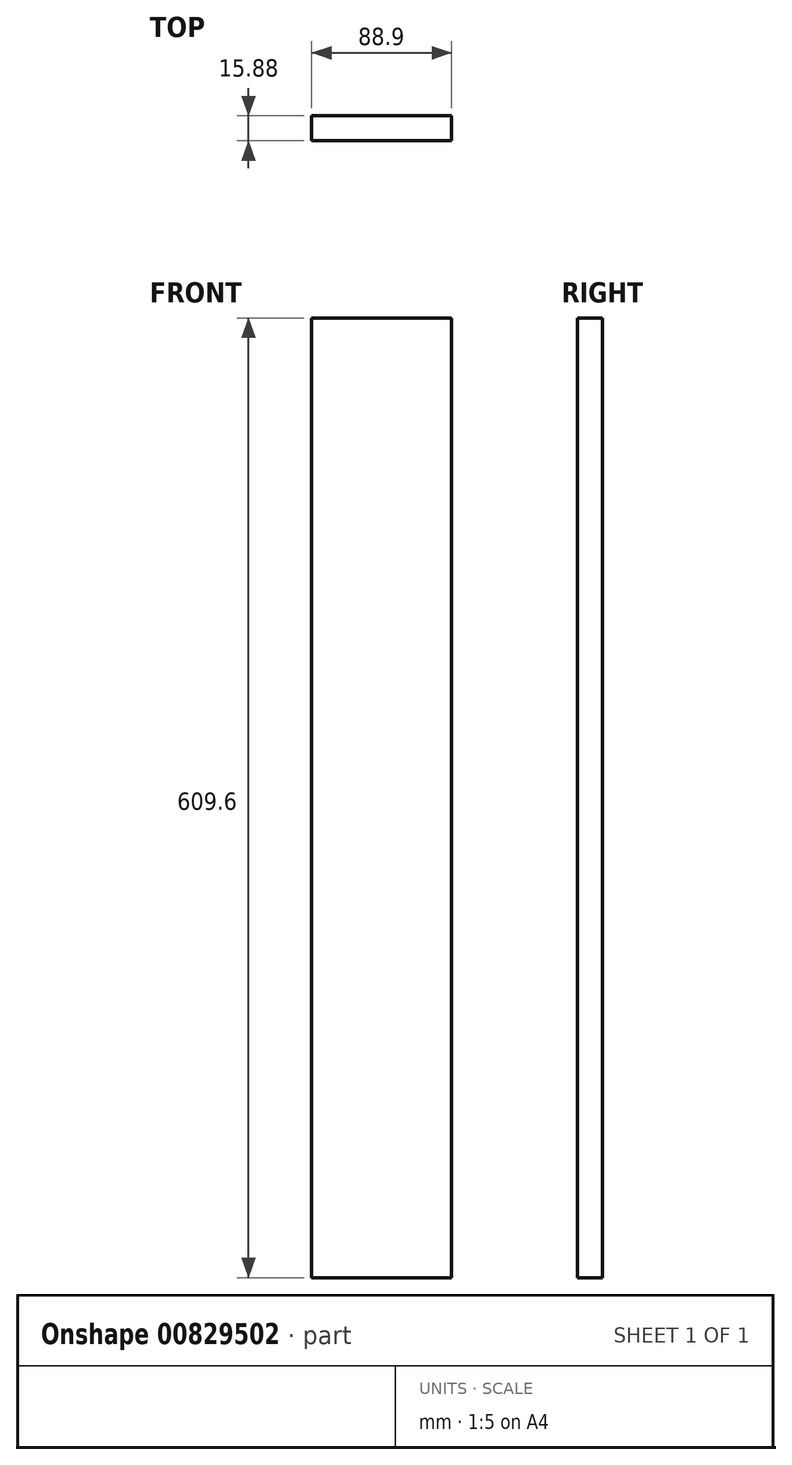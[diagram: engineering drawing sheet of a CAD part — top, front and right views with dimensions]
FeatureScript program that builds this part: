
annotation { "Feature Type Name" : "Feature", "Feature Type Description" : "" }
export const myFeature = defineFeature(function(context is Context, id is Id, definition is map)
    precondition{}
    {
        {
            var Q0;
            Q0=qCreatedBy(makeId("Top.planeOp"),FACE);
            var sketch = newSketch(context, id + "F0", { "sketchPlane" : qUnion([Q0])});
            skLineSegment(sketch, "E0.bottom", {"start": v(0, 0) * mm, "end": v(88.9, 0) * mm});
            skLineSegment(sketch, "E0.top", {"start": v(0, -15.88) * mm, "end": v(88.9, -15.88) * mm});
            skLineSegment(sketch, "E0.left", {"start": v(0, 0) * mm, "end": v(0, -15.88) * mm});
            skLineSegment(sketch, "E0.right", {"start": v(88.9, 0) * mm, "end": v(88.9, -15.88) * mm});
            skSolve(sketch);
        }
        {
            var Q0;
            Q0 = qSketchRegion(id + "F0", true);
            extrude(context, id + "F1", {"entities" : qUnion([Q0]), "depth" : 609.6 * mm, "offsetDistance" : 25.4 * mm});
        }
    });
